# Revit family: Cleanout-Zurn-Z1406-Heavy Duty
name_source: partatom
category: Plumbing Fixtures
units: mm (PartAtom-declared; Revit-internal decimal feet)

## family parameters
Always vertical = Yes
Cut with Voids When Loaded = No
Maintain Annotation Orientation = No
OmniClass Number = 23.70.50.21.24.14
OmniClass Title = Deck Waste Water Drains
Part Type = Normal
Room Calculation Point = No
Round Connector Dimension = Use Radius
Shared = No
Work Plane-Based = No

## types (9) — shared parameters
Assembly Code = D2030100
CW Connection = No
Default Elevation = 20 "
Description = HEAVY-DUTY SPIGOT CLEANOUT ADJUSTABLE
Enter Value-Frame Adjustment Height = 10 "
HW Connection = No
Main Material = Iron - Zurn - Cast - Painted - Blue
Manufacturer = Zurn Water, LLC
Manufacurer Brand = Zurn
Modified Date = 01/06/2025
Product Documentation Link = https://files.zurn.com
Product Installation Sheet URL = https://files.zurn.com
Product Page URL = https://www.zurn.com
Product data url = https://www.bimobject.com
URL = www.zurn.com
Vent Connection = No
WFU = 1
Waste Connection = Yes
zero-valued in all types: CWFU, HWFU

## per-type parameters (varying)
| type | Approx. Weight (Lbs) | Connector Radius | Dimension "B" | Dimension "C" | Grate Radius | Model | Pipe Size_A Inside Diameter | Pipe Size_A Nominal Diameter | Pipe Size_A Outer Diameter | Top Material | Type Comments | ZN/ZS Top value |
| Z1406-3SP | 11 " | 1.5 " | 2 " | 6.125 " | 5.525 " | Z1406 | 3.068 " | 3 " | 3.5 " | Iron - Zurn - Cast - Painted - Blue | Z1406 With 3 Inch Spigot Connection | 0 " |
| Z1406-4SP | 15 " | 2 " | 3.5 " | 7.25 " | 6.65 " | Z1406 | 4.026 " | 4 " | 4.5 " | Iron - Zurn - Cast - Painted - Blue | Z1406 With 4 Inch Spigot Connection | 0 " |
| Z1406-6SP | 23 " | 3 " | 3.5 " | 9.25 " | 8.65 " | Z1406 | 6.065 " | 6 " | 6.625 " | Iron - Zurn - Cast - Painted - Blue | Z1406 With 6 Inch Spigot Connection | 0 " |
| ZN1406-3SP | 11 " | 1.5 " | 2 " | 6.125 " | 5.525 " | ZN1406 | 3.068 " | 3 " | 3.5 " | Bronze - Zurn - Polished Nickel | ZN1406 With 3 Inch Spigot Connection | 0.5 " |
| ZN1406-4SP | 15 " | 2 " | 3.5 " | 7.25 " | 6.65 " | ZN1406 | 4.026 " | 4 " | 4.5 " | Bronze - Zurn - Polished Nickel | ZN1406 With 4 Inch Spigot Connection | 0.5 " |
| ZN1406-6SP | 23 " | 3 " | 3.5 " | 9.25 " | 8.65 " | ZN1406 | 6.065 " | 6 " | 6.625 " | Bronze - Zurn - Polished Nickel | ZN1406 With 6 Inch Spigot Connection | 0.5 " |
| ZS1406-3ZS | 11 " | 1.5 " | 2 " | 6.125 " | 5.525 " | ZS1406 | 3.068 " | 3 " | 3.5 " | Steel - Zurn - Stainless - Type - 304 | ZN1406 With 3 Inch Spigot Connection | -0.188 " |
| ZS1406-4ZS | 15 " | 2 " | 3.5 " | 7.25 " | 6.65 " | ZS1406 | 4.026 " | 4 " | 4.5 " | Steel - Zurn - Stainless - Type - 304 | ZN1406 With 4 Inch Spigot Connection | -0.188 " |
| ZS1406-6ZS | 23 " | 3 " | 3.5 " | 9.25 " | 8.65 " | ZS1406 | 6.065 " | 6 " | 6.625 " | Steel - Zurn - Stainless - Type - 304 | ZN1406 With 6 Inch Spigot Connection | -0.188 " |

## geometry (parser evidence)
native form markers: Sweep x3
no freeform markers — native parametric forms only
